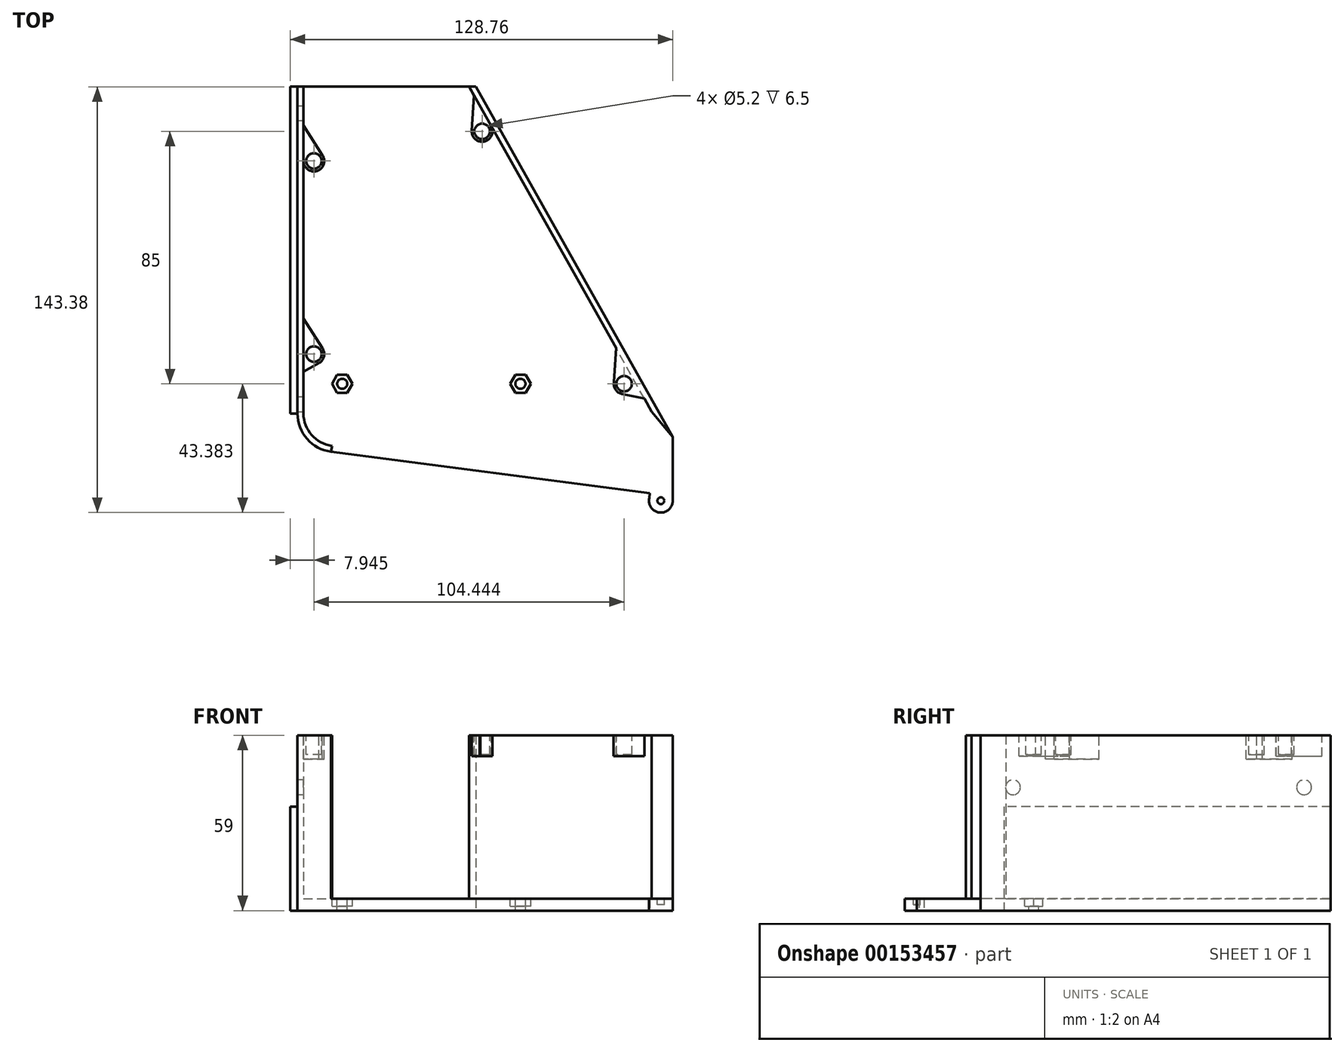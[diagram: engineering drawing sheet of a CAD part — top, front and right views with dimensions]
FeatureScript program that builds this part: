
annotation { "Feature Type Name" : "Feature", "Feature Type Description" : "" }
export const myFeature = defineFeature(function(context is Context, id is Id, definition is map)
    precondition{}
    {
        {
            var Q0;
            Q0=qCreatedBy(makeId("Top.planeOp"),FACE);
            var sketch = newSketch(context, id + "F0", { "sketchPlane" : qUnion([Q0])});
            skLineSegment(sketch, "E0", {"start": v(-60.03, 83.64) * mm, "end": v(-60.03, -26.36) * mm});
            skLineSegment(sketch, "E1", {"start": v(-48.72, -39.25) * mm, "end": v(66.28, -54.25) * mm});
            skLineSegment(sketch, "E2", {"start": v(66.28, -34.25) * mm, "end": v(-0.03, 83.64) * mm});
            skLineSegment(sketch, "E3", {"start": v(-60.03, 83.64) * mm, "end": v(-0.03, 83.64) * mm});
            skLineSegment(sketch, "E4", {"start": v(66.28, -34.25) * mm, "end": v(66.28, -54.25) * mm});
            skPoint(sketch, "E5.visualSharp", {"position": v(-60.03, -37.77) * mm});
            skArc(sketch, "E5.filletArc", {"start": v(-60.03, -26.36) * mm, "mid": v(-56.8, -34.93) * mm, "end": v(-48.72, -39.25) * mm});
            skCircle(sketch, "E6", {"center": v(62.28, -55.74) * mm, "radius": 4 * mm});
            skLineSegment(sketch, "E7", {"start": v(66.28, -55.79) * mm, "end": v(66.28, -54.25) * mm});
            skLineSegment(sketch, "E8", {"start": v(58.37, -54.91) * mm, "end": v(58.59, -53.24) * mm});
            skSolve(sketch);
        }
        {
            var Q0;
            Q0 = qSketchRegion(id + "F0", true);
            var Q1;
            {var subQ0=sQuery(id+"F0.wireOp",EDGE,"E6");var subQ1=sQuery(id+"F0.wireOp",EDGE,"E1");var subQ2=makeQuery(id+"F0.imprint","INTERSECT",VERTEX,{"disambiguationData":[OD(0.0)],"derivedFrom":[subQ1,subQ0]});Q1=makeQuery(id+"F0.imprint","IMPRINT",FACE,{"disambiguationData":[TD([[makeQuery(id+"F0.imprint","IMPRINT",EDGE,{"disambiguationData":[TD([[subQ2,-1.0]])],"derivedFrom":subQ1}),1.0]])]});}
            extrude(context, id + "F1", {"entities" : qUnion([Q0, Q1]), "depth" : 4 * mm});
        }
        {
            var Q0;
            Q0=makeQuery(id+"F1.opExtrude","CAP_FACE",FACE,{"disambiguationData":[OSD([sQuery(id+"F0.wireOp",EDGE,"E0"),sQuery(id+"F0.wireOp",EDGE,"E1"),sQuery(id+"F0.wireOp",EDGE,"E2"),sQuery(id+"F0.wireOp",EDGE,"E3"),sQuery(id+"F0.wireOp",EDGE,"E4"),sQuery(id+"F0.wireOp",EDGE,"E5.filletArc")])],"isStart":false});
            var sketch = newSketch(context, id + "F2", { "sketchPlane" : qUnion([Q0])});
            skLineSegment(sketch, "E9.0", {"start": v(-48.46, -37.26) * mm, "end": v(52.4, -50.42) * mm});
            skArc(sketch, "E9.1", {"start": v(-58.03, -26.36) * mm, "mid": v(-55.3, -33.61) * mm, "end": v(-48.46, -37.26) * mm});
            skLineSegment(sketch, "E9.2", {"start": v(-58.03, 83.64) * mm, "end": v(-58.03, -26.36) * mm});
            skLineSegment(sketch, "E10", {"start": v(66.28, -54.25) * mm, "end": v(66.28, -52.23) * mm});
            skLineSegment(sketch, "E11", {"start": v(-60.03, 83.64) * mm, "end": v(-58.03, 83.64) * mm});
            skLineSegment(sketch, "E12", {"start": v(-48.46, -37.26) * mm, "end": v(-48.72, -39.25) * mm});
            skLineSegment(sketch, "E13.0", {"start": v(59.2, -25.73) * mm, "end": v(-2.7, 84.31) * mm});
            skLineSegment(sketch, "E14", {"start": v(-2.33, 83.64) * mm, "end": v(-2.7, 84.31) * mm});
            skLineSegment(sketch, "E15", {"start": v(59.2, -25.73) * mm, "end": v(66.28, -34.25) * mm});
            skSolve(sketch);
        }
        {
            var Q0;
            Q0 = qSketchRegion(id + "F2", true);
            var Q1;
            Q1=makeQuery(id+"F2.imprint","IMPRINT",FACE,{"disambiguationData":[TD([[makeQuery(id+"F2.imprint","IMPRINT",EDGE,{"derivedFrom":sQuery(id+"F2.wireOp",EDGE,"E9.1")}),-1.0]])]});
            var Q2;
            {var subQ2=sQuery(id+"F2.wireOp",EDGE,"E14");Q2=makeQuery(id+"F2.imprint","IMPRINT",FACE,{"disambiguationData":[TD([[makeQuery(id+"F2.imprint","IMPRINT",EDGE,{"derivedFrom":subQ2}),-1.0]])]});}
            var Q3;
            {var subQ0=sQuery(id+"F2.wireOp",EDGE,"E13.0");Q3=makeQuery(id+"F2.imprint","IMPRINT",FACE,{"disambiguationData":[TD([[makeQuery(id+"F2.imprint","IMPRINT",EDGE,{"derivedFrom":subQ0}),-1.0]])]});}
            extrude(context, id + "F3", {"entities" : qUnion([Q0, Q1, Q2, Q3]), "operationType" : NewBodyOperationType.ADD, "depth" : 55 * mm});
        }
        {
            var Q0;
            {var subQ0=sQuery(id+"F0.wireOp",EDGE,"E0");Q0=makeQuery(id+"F3.boolean.opBoolean","MERGE",FACE,{"derivedFrom":[makeQuery(id+"F1.opExtrude","SWEPT_FACE",FACE,{"disambiguationData":[OSD([subQ0])]}),makeQuery(id+"F3.opExtrude","SWEPT_FACE",FACE,{"disambiguationData":[OSD([subQ0])]})]});}
            var sketch = newSketch(context, id + "F4", { "sketchPlane" : qUnion([Q0])});
            skCircle(sketch, "E16", {"center": v(23.36, 41.5) * mm, "radius": 2.5 * mm});
            skCircle(sketch, "E17", {"center": v(-74.64, 41.5) * mm, "radius": 2.5 * mm});
            skSolve(sketch);
        }
        {
            var Q0;
            Q0 = qSketchRegion(id + "F4", true);
            extrude(context, id + "F5", {"entities" : qUnion([Q0]), "operationType" : NewBodyOperationType.REMOVE, "endBound" : BoundingType.UP_TO_NEXT, "oppositeDirection" : true, "depth" : 25 * mm});
        }
        {
            var Q0;
            Q0=makeQuery(id+"F1.opExtrude","CAP_FACE",FACE,{"disambiguationData":[OSD([sQuery(id+"F0.wireOp",EDGE,"E0"),sQuery(id+"F0.wireOp",EDGE,"E1"),sQuery(id+"F0.wireOp",EDGE,"E2"),sQuery(id+"F0.wireOp",EDGE,"E3"),sQuery(id+"F0.wireOp",EDGE,"E4"),sQuery(id+"F0.wireOp",EDGE,"E5.filletArc"),sQuery(id+"F0.wireOp",EDGE,"E6"),sQuery(id+"F0.wireOp",EDGE,"E7"),sQuery(id+"F0.wireOp",EDGE,"E8")])],"isStart":false});
            var sketch = newSketch(context, id + "F6", { "sketchPlane" : qUnion([Q0])});
            skCircle(sketch, "E18", {"center": v(62.28, -55.74) * mm, "radius": 1.15 * mm});
            skSolve(sketch);
        }
        {
            var Q0;
            Q0 = qSketchRegion(id + "F6", true);
            extrude(context, id + "F7", {"entities" : qUnion([Q0]), "operationType" : NewBodyOperationType.REMOVE, "oppositeDirection" : true, "depth" : 2 * mm});
        }
        {
            var Q0;
            Q0=makeQuery(id+"F1.opExtrude","CAP_FACE",FACE,{"disambiguationData":[OSD([sQuery(id+"F0.wireOp",EDGE,"E0"),sQuery(id+"F0.wireOp",EDGE,"E1"),sQuery(id+"F0.wireOp",EDGE,"E2"),sQuery(id+"F0.wireOp",EDGE,"E3"),sQuery(id+"F0.wireOp",EDGE,"E4"),sQuery(id+"F0.wireOp",EDGE,"E5.filletArc"),sQuery(id+"F0.wireOp",EDGE,"E6"),sQuery(id+"F0.wireOp",EDGE,"E7"),sQuery(id+"F0.wireOp",EDGE,"E8")])],"isStart":false});
            var sketch = newSketch(context, id + "F8", { "sketchPlane" : qUnion([Q0])});
            skCircle(sketch, "E19.cCircle", {"center": v(-45, -16.36) * mm, "radius": 3 * mm, "construction": true});
            skLineSegment(sketch, "E19.0", {"start": v(-46.73, -13.36) * mm, "end": v(-43.26, -13.36) * mm});
            skLineSegment(sketch, "E19.1", {"start": v(-43.26, -13.36) * mm, "end": v(-41.53, -16.36) * mm});
            skLineSegment(sketch, "E19.2", {"start": v(-41.53, -16.36) * mm, "end": v(-43.26, -19.36) * mm});
            skLineSegment(sketch, "E19.3", {"start": v(-43.26, -19.36) * mm, "end": v(-46.73, -19.36) * mm});
            skLineSegment(sketch, "E19.4", {"start": v(-46.73, -19.36) * mm, "end": v(-48.46, -16.36) * mm});
            skLineSegment(sketch, "E19.5", {"start": v(-48.46, -16.36) * mm, "end": v(-46.73, -13.36) * mm});
            skPoint(sketch, "E19.0.midPoint", {"position": v(-45, -13.36) * mm});
            skCircle(sketch, "E20.cCircle", {"center": v(15, -16.36) * mm, "radius": 3 * mm, "construction": true});
            skLineSegment(sketch, "E20.0", {"start": v(13.27, -13.36) * mm, "end": v(16.74, -13.36) * mm});
            skLineSegment(sketch, "E20.1", {"start": v(16.74, -13.36) * mm, "end": v(18.47, -16.36) * mm});
            skLineSegment(sketch, "E20.2", {"start": v(18.47, -16.36) * mm, "end": v(16.74, -19.36) * mm});
            skLineSegment(sketch, "E20.3", {"start": v(16.74, -19.36) * mm, "end": v(13.27, -19.36) * mm});
            skLineSegment(sketch, "E20.4", {"start": v(13.27, -19.36) * mm, "end": v(11.54, -16.36) * mm});
            skLineSegment(sketch, "E20.5", {"start": v(11.54, -16.36) * mm, "end": v(13.27, -13.36) * mm});
            skPoint(sketch, "E20.0.midPoint", {"position": v(15, -13.36) * mm});
            skSolve(sketch);
        }
        {
            var Q0;
            Q0 = qSketchRegion(id + "F8", true);
            extrude(context, id + "F9", {"entities" : qUnion([Q0]), "operationType" : NewBodyOperationType.REMOVE, "oppositeDirection" : true, "depth" : 2.5 * mm});
        }
        {
            var Q0;
            Q0=makeQuery(id+"F9.boolean.opBoolean","COPY",FACE,{"derivedFrom":makeQuery(id+"F9.opExtrude","CAP_FACE",FACE,{"disambiguationData":[OSD([sQuery(id+"F8.wireOp",EDGE,"E20.0"),sQuery(id+"F8.wireOp",EDGE,"E20.1"),sQuery(id+"F8.wireOp",EDGE,"E20.2"),sQuery(id+"F8.wireOp",EDGE,"E20.3"),sQuery(id+"F8.wireOp",EDGE,"E20.4"),sQuery(id+"F8.wireOp",EDGE,"E20.5")])],"isStart":false})});
            var sketch = newSketch(context, id + "F10", { "sketchPlane" : qUnion([Q0])});
            skCircle(sketch, "E21", {"center": v(15, -16.36) * mm, "radius": 1.7 * mm});
            skSolve(sketch);
        }
        {
            var Q0;
            Q0 = qSketchRegion(id + "F10", true);
            extrude(context, id + "F11", {"entities" : qUnion([Q0]), "operationType" : NewBodyOperationType.REMOVE, "endBound" : BoundingType.UP_TO_NEXT, "oppositeDirection" : true, "depth" : 25 * mm});
        }
        {
            var Q0;
            Q0=makeQuery(id+"F9.boolean.opBoolean","COPY",FACE,{"derivedFrom":makeQuery(id+"F9.opExtrude","CAP_FACE",FACE,{"disambiguationData":[OSD([sQuery(id+"F8.wireOp",EDGE,"E19.0"),sQuery(id+"F8.wireOp",EDGE,"E19.1"),sQuery(id+"F8.wireOp",EDGE,"E19.2"),sQuery(id+"F8.wireOp",EDGE,"E19.3"),sQuery(id+"F8.wireOp",EDGE,"E19.4"),sQuery(id+"F8.wireOp",EDGE,"E19.5")])],"isStart":false})});
            var sketch = newSketch(context, id + "F12", { "sketchPlane" : qUnion([Q0])});
            skCircle(sketch, "E22", {"center": v(-45, -16.36) * mm, "radius": 1.7 * mm});
            skSolve(sketch);
        }
        {
            var Q0;
            Q0 = qSketchRegion(id + "F12", true);
            extrude(context, id + "F13", {"entities" : qUnion([Q0]), "operationType" : NewBodyOperationType.REMOVE, "endBound" : BoundingType.UP_TO_NEXT, "oppositeDirection" : true, "depth" : 25 * mm});
        }
        {
            var Q0;
            Q0=makeQuery(id+"F3.opExtrude","CAP_FACE",FACE,{"disambiguationData":[OSD([sQuery(id+"F0.wireOp",EDGE,"E0"),sQuery(id+"F0.wireOp",EDGE,"E5.filletArc"),sQuery(id+"F2.wireOp",EDGE,"E9.1"),sQuery(id+"F2.wireOp",EDGE,"E9.2"),sQuery(id+"F2.wireOp",EDGE,"E11"),sQuery(id+"F2.wireOp",EDGE,"E12")])],"isStart":false});
            var sketch = newSketch(context, id + "F14", { "sketchPlane" : qUnion([Q0])});
            skCircle(sketch, "E23", {"center": v(-54.53, -6.36) * mm, "radius": 3.5 * mm});
            skLineSegment(sketch, "E24", {"start": v(-51.48, -4.64) * mm, "end": v(-58.03, 5.64) * mm});
            skLineSegment(sketch, "E25", {"start": v(-52.77, -9.38) * mm, "end": v(-58.03, -12.36) * mm});
            skCircle(sketch, "E26", {"center": v(-54.53, 58.64) * mm, "radius": 3.5 * mm});
            skLineSegment(sketch, "E27", {"start": v(-51.64, 60.61) * mm, "end": v(-58.03, 70.64) * mm});
            skLineSegment(sketch, "E28", {"start": v(-53.23, 55.4) * mm, "end": v(-58.03, 53.64) * mm});
            skSolve(sketch);
        }
        {
            var Q0;
            Q0 = qSketchRegion(id + "F14", true);
            var Q1;
            {var subQ0=sQuery(id+"F14.wireOp",EDGE,"E24");Q1=makeQuery(id+"F14.imprint","IMPRINT",FACE,{"disambiguationData":[TD([[makeQuery(id+"F14.imprint","IMPRINT",EDGE,{"derivedFrom":subQ0}),1.0]])]});}
            var Q2;
            {var subQ0=sQuery(id+"F14.wireOp",EDGE,"E25");Q2=makeQuery(id+"F14.imprint","IMPRINT",FACE,{"disambiguationData":[TD([[makeQuery(id+"F14.imprint","IMPRINT",EDGE,{"derivedFrom":subQ0}),-1.0]])]});}
            var Q3;
            {var subQ0=sQuery(id+"F14.wireOp",EDGE,"E27");Q3=makeQuery(id+"F14.imprint","IMPRINT",FACE,{"disambiguationData":[TD([[makeQuery(id+"F14.imprint","IMPRINT",EDGE,{"derivedFrom":subQ0}),1.0]])]});}
            var Q4;
            {var subQ0=sQuery(id+"F14.wireOp",EDGE,"E28");var subQ1=sQuery(id+"F14.wireOp",EDGE,"E26");var subQ2=makeQuery(id+"F14.imprint","INTERSECT",VERTEX,{"disambiguationData":[OD(1.0)],"derivedFrom":[subQ1,subQ0]});Q4=makeQuery(id+"F14.imprint","IMPRINT",FACE,{"disambiguationData":[TD([[makeQuery(id+"F14.imprint","IMPRINT",EDGE,{"disambiguationData":[TD([[subQ2,1.0]])],"derivedFrom":subQ1}),-1.0]])]});}
            extrude(context, id + "F15", {"entities" : qUnion([Q0, Q1, Q2, Q3, Q4]), "operationType" : NewBodyOperationType.ADD, "oppositeDirection" : true, "depth" : 8 * mm});
        }
        {
            var Q0;
            Q0=makeQuery(id+"F3.opExtrude","CAP_FACE",FACE,{"disambiguationData":[OSD([sQuery(id+"F0.wireOp",EDGE,"E2"),sQuery(id+"F0.wireOp",EDGE,"E3"),sQuery(id+"F2.wireOp",EDGE,"E13.0"),sQuery(id+"F2.wireOp",EDGE,"E15")])],"isStart":false});
            var sketch = newSketch(context, id + "F16", { "sketchPlane" : qUnion([Q0])});
            skCircle(sketch, "E29", {"center": v(2.1, 68.64) * mm, "radius": 3.5 * mm});
            skLineSegment(sketch, "E30", {"start": v(-1.4, 68.87) * mm, "end": v(-0.64, 80.64) * mm});
            skLineSegment(sketch, "E31", {"start": v(1.24, 65.25) * mm, "end": v(8.92, 63.64) * mm});
            skCircle(sketch, "E32", {"center": v(49.9, -16.36) * mm, "radius": 3.5 * mm});
            skLineSegment(sketch, "E33", {"start": v(46.47, -15.72) * mm, "end": v(47.17, -4.36) * mm});
            skLineSegment(sketch, "E34", {"start": v(49.2, -19.78) * mm, "end": v(56.74, -21.36) * mm});
            skSolve(sketch);
        }
        {
            var Q0;
            {var subQ0=sQuery(id+"F16.wireOp",EDGE,"E33");var subQ1=sQuery(id+"F16.wireOp",EDGE,"E32");var subQ2=makeQuery(id+"F16.imprint","INTERSECT",VERTEX,{"disambiguationData":[OD(1.0)],"derivedFrom":[subQ1,subQ0]});Q0=makeQuery(id+"F16.imprint","IMPRINT",FACE,{"disambiguationData":[TD([[makeQuery(id+"F16.imprint","IMPRINT",EDGE,{"disambiguationData":[TD([[subQ2,1.0]])],"derivedFrom":subQ1}),1.0]])]});}
            var Q1;
            {var subQ0=sQuery(id+"F16.wireOp",EDGE,"E33");var subQ1=sQuery(id+"F16.wireOp",EDGE,"E32");var subQ2=makeQuery(id+"F16.imprint","INTERSECT",VERTEX,{"disambiguationData":[OD(1.0)],"derivedFrom":[subQ1,subQ0]});Q1=makeQuery(id+"F16.imprint","IMPRINT",FACE,{"disambiguationData":[TD([[makeQuery(id+"F16.imprint","IMPRINT",EDGE,{"disambiguationData":[TD([[subQ2,1.0]])],"derivedFrom":subQ1}),-1.0]])]});}
            var Q2;
            {var subQ0=sQuery(id+"F16.wireOp",EDGE,"E34");Q2=makeQuery(id+"F16.imprint","IMPRINT",FACE,{"disambiguationData":[TD([[makeQuery(id+"F16.imprint","IMPRINT",EDGE,{"derivedFrom":subQ0}),1.0]])]});}
            var Q3;
            {var subQ0=sQuery(id+"F16.wireOp",EDGE,"E29");var subQ1=makeQuery(id+"F16.imprint","INTERSECT",VERTEX,{"derivedFrom":[subQ0,sQuery(id+"F16.wireOp",EDGE,"E30")]});Q3=makeQuery(id+"F16.imprint","IMPRINT",FACE,{"disambiguationData":[TD([[makeQuery(id+"F16.imprint","IMPRINT",EDGE,{"disambiguationData":[TD([[subQ1,1.0]])],"derivedFrom":subQ0}),1.0]])]});}
            var Q4;
            {var subQ0=sQuery(id+"F16.wireOp",EDGE,"E31");var subQ1=sQuery(id+"F16.wireOp",EDGE,"E29");var subQ2=makeQuery(id+"F16.imprint","INTERSECT",VERTEX,{"disambiguationData":[OD(1.0)],"derivedFrom":[subQ1,subQ0]});Q4=makeQuery(id+"F16.imprint","IMPRINT",FACE,{"disambiguationData":[TD([[makeQuery(id+"F16.imprint","IMPRINT",EDGE,{"disambiguationData":[TD([[subQ2,-1.0]])],"derivedFrom":subQ1}),-1.0]])]});}
            var Q5;
            {var subQ0=sQuery(id+"F16.wireOp",EDGE,"E30");Q5=makeQuery(id+"F16.imprint","IMPRINT",FACE,{"disambiguationData":[TD([[makeQuery(id+"F16.imprint","IMPRINT",EDGE,{"derivedFrom":subQ0}),-1.0]])]});}
            extrude(context, id + "F17", {"entities" : qUnion([Q0, Q1, Q2, Q3, Q4, Q5]), "operationType" : NewBodyOperationType.ADD, "oppositeDirection" : true, "depth" : 7 * mm});
        }
        {
            var Q0;
            {var subQ0=sQuery(id+"F2.wireOp",EDGE,"E9.2");Q0=makeQuery(id+"F15.boolean.opBoolean","MERGE",FACE,{"derivedFrom":[makeQuery(id+"F3.opExtrude","CAP_FACE",FACE,{"disambiguationData":[OSD([sQuery(id+"F0.wireOp",EDGE,"E0"),sQuery(id+"F0.wireOp",EDGE,"E5.filletArc"),sQuery(id+"F2.wireOp",EDGE,"E9.1"),subQ0,sQuery(id+"F2.wireOp",EDGE,"E11"),sQuery(id+"F2.wireOp",EDGE,"E12")])],"isStart":false}),makeQuery(id+"F15.opExtrude","CAP_FACE",FACE,{"disambiguationData":[OSD([subQ0,sQuery(id+"F14.wireOp",EDGE,"E23"),sQuery(id+"F14.wireOp",EDGE,"E24"),sQuery(id+"F14.wireOp",EDGE,"E25")])],"isStart":true}),makeQuery(id+"F15.opExtrude","CAP_FACE",FACE,{"disambiguationData":[OSD([subQ0,sQuery(id+"F14.wireOp",EDGE,"E26"),sQuery(id+"F14.wireOp",EDGE,"E27"),sQuery(id+"F14.wireOp",EDGE,"E28")])],"isStart":true})]});}
            var sketch = newSketch(context, id + "F18", { "sketchPlane" : qUnion([Q0])});
            skCircle(sketch, "E35", {"center": v(-54.53, -6.36) * mm, "radius": 2.6 * mm});
            skCircle(sketch, "E36", {"center": v(-54.53, 58.64) * mm, "radius": 2.6 * mm});
            skSolve(sketch);
        }
        {
            var Q0;
            Q0 = qSketchRegion(id + "F18", true);
            extrude(context, id + "F19", {"entities" : qUnion([Q0]), "operationType" : NewBodyOperationType.REMOVE, "oppositeDirection" : true, "depth" : 6.5 * mm});
        }
        {
            var Q0;
            {var subQ0=sQuery(id+"F2.wireOp",EDGE,"E13.0");Q0=makeQuery(id+"F17.boolean.opBoolean","MERGE",FACE,{"derivedFrom":[makeQuery(id+"F3.opExtrude","CAP_FACE",FACE,{"disambiguationData":[OSD([sQuery(id+"F0.wireOp",EDGE,"E2"),sQuery(id+"F0.wireOp",EDGE,"E3"),subQ0,sQuery(id+"F2.wireOp",EDGE,"E15")])],"isStart":false}),makeQuery(id+"F17.opExtrude","CAP_FACE",FACE,{"disambiguationData":[OSD([subQ0,sQuery(id+"F16.wireOp",EDGE,"E29"),sQuery(id+"F16.wireOp",EDGE,"E30"),sQuery(id+"F16.wireOp",EDGE,"E31")])],"isStart":true}),makeQuery(id+"F17.opExtrude","CAP_FACE",FACE,{"disambiguationData":[OSD([subQ0,sQuery(id+"F16.wireOp",EDGE,"E32"),sQuery(id+"F16.wireOp",EDGE,"E33"),sQuery(id+"F16.wireOp",EDGE,"E34")])],"isStart":true})]});}
            var sketch = newSketch(context, id + "F20", { "sketchPlane" : qUnion([Q0])});
            skCircle(sketch, "E37", {"center": v(49.9, -16.36) * mm, "radius": 2.6 * mm});
            skCircle(sketch, "E38", {"center": v(2.1, 68.64) * mm, "radius": 2.6 * mm});
            skSolve(sketch);
        }
        {
            var Q0;
            Q0 = qSketchRegion(id + "F20", true);
            extrude(context, id + "F21", {"entities" : qUnion([Q0]), "operationType" : NewBodyOperationType.REMOVE, "oppositeDirection" : true, "depth" : 6.5 * mm});
        }
        {
            var Q0;
            {var subQ0=sQuery(id+"F0.wireOp",EDGE,"E0");Q0=makeQuery(id+"F3.boolean.opBoolean","MERGE",FACE,{"derivedFrom":[makeQuery(id+"F1.opExtrude","SWEPT_FACE",FACE,{"disambiguationData":[OSD([subQ0])]}),makeQuery(id+"F3.opExtrude","SWEPT_FACE",FACE,{"disambiguationData":[OSD([subQ0])]})]});}
            var sketch = newSketch(context, id + "F22", { "sketchPlane" : qUnion([Q0])});
            skLineSegment(sketch, "E39.bottom", {"start": v(-83.64, 0) * mm, "end": v(26.36, 0) * mm});
            skLineSegment(sketch, "E39.top", {"start": v(-83.64, 35) * mm, "end": v(26.36, 35) * mm});
            skLineSegment(sketch, "E39.left", {"start": v(-83.64, 0) * mm, "end": v(-83.64, 35) * mm});
            skLineSegment(sketch, "E39.right", {"start": v(26.36, 0) * mm, "end": v(26.36, 35) * mm});
            skSolve(sketch);
        }
        {
            var Q0;
            Q0 = qSketchRegion(id + "F22", true);
            extrude(context, id + "F23", {"entities" : qUnion([Q0]), "operationType" : NewBodyOperationType.ADD, "depth" : 2.45 * mm});
        }
    });
